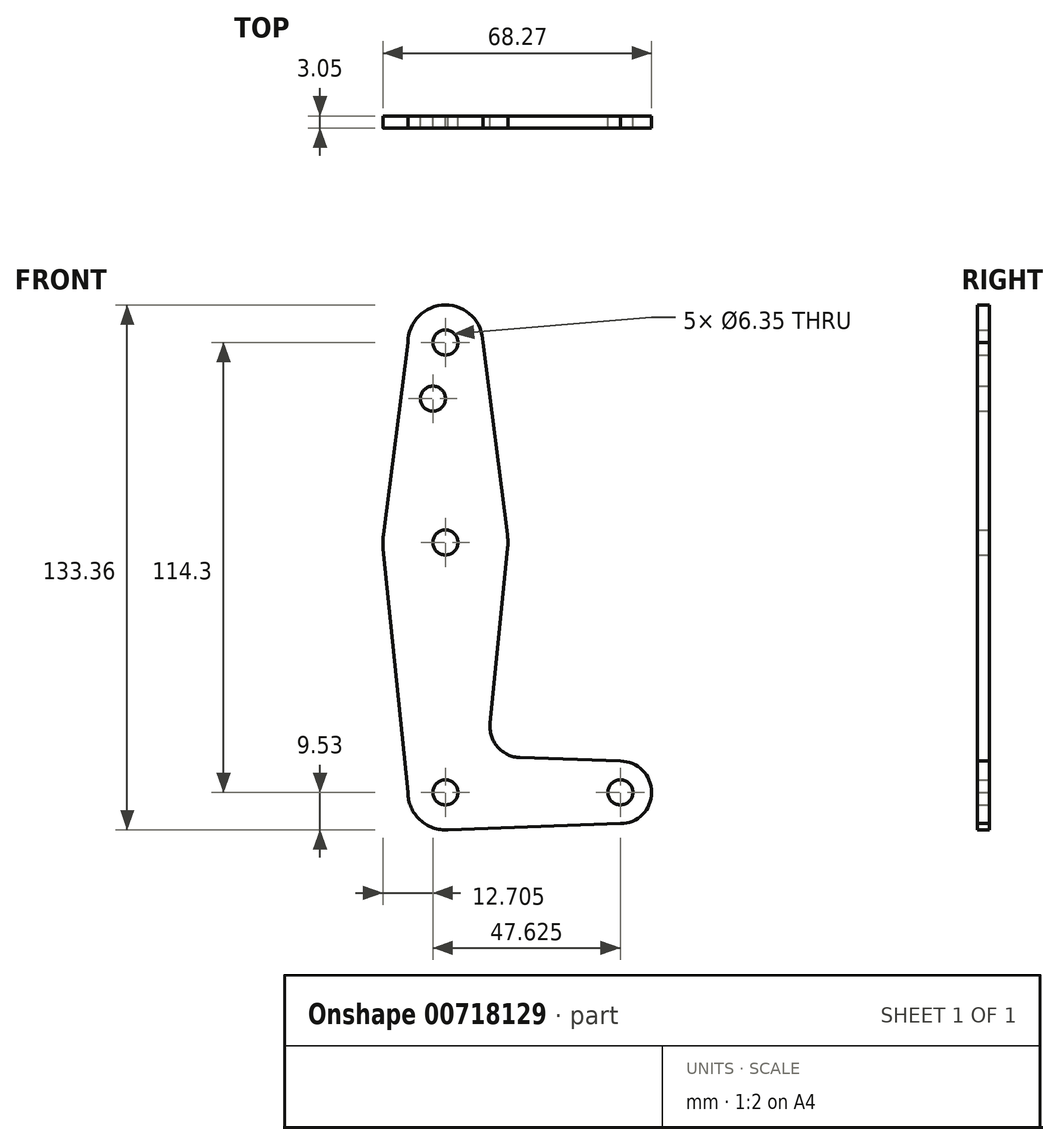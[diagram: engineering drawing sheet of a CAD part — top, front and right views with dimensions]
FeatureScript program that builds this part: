
annotation { "Feature Type Name" : "Feature", "Feature Type Description" : "" }
export const myFeature = defineFeature(function(context is Context, id is Id, definition is map)
    precondition{}
    {
        {
            var Q0;
            Q0=qCreatedBy(makeId("Front.planeOp"),FACE);
            var sketch = newSketch(context, id + "F0", { "sketchPlane" : qUnion([Q0])});
            skLineSegment(sketch, "E0", {"start": v(0, 0) * mm, "end": v(44.45, 0) * mm});
            skLineSegment(sketch, "E1", {"start": v(0, 0) * mm, "end": v(0, 63.5) * mm});
            skLineSegment(sketch, "E2", {"start": v(0, 63.5) * mm, "end": v(0, 114.3) * mm});
            skCircle(sketch, "E3", {"center": v(0, 114.3) * mm, "radius": 9.53 * mm});
            skCircle(sketch, "E4", {"center": v(0, 63.5) * mm, "radius": 15.88 * mm});
            skCircle(sketch, "E5", {"center": v(0, 0) * mm, "radius": 9.53 * mm});
            skCircle(sketch, "E6", {"center": v(44.45, 0) * mm, "radius": 7.94 * mm});
            skLineSegment(sketch, "E7", {"start": v(-9.53, 114.3) * mm, "end": v(-15.75, 65.5) * mm});
            skLineSegment(sketch, "E8", {"start": v(9.53, 114.3) * mm, "end": v(15.75, 65.5) * mm});
            skLineSegment(sketch, "E9", {"start": v(15.8, 61.91) * mm, "end": v(11.34, 17.59) * mm});
            skLineSegment(sketch, "E10", {"start": v(-15.8, 61.91) * mm, "end": v(-9.52, 0) * mm});
            skLineSegment(sketch, "E11", {"start": v(18.97, 8.85) * mm, "end": v(44.45, 7.94) * mm});
            skLineSegment(sketch, "E12", {"start": v(0, -9.53) * mm, "end": v(44.45, -7.94) * mm});
            skCircle(sketch, "E13", {"center": v(-3.18, 100.03) * mm, "radius": 3.18 * mm});
            skCircle(sketch, "E14", {"center": v(0, 114.3) * mm, "radius": 3.18 * mm});
            skCircle(sketch, "E15", {"center": v(0, 63.5) * mm, "radius": 3.18 * mm});
            skCircle(sketch, "E16", {"center": v(0, 0) * mm, "radius": 3.18 * mm});
            skCircle(sketch, "E17", {"center": v(44.45, 0) * mm, "radius": 3.18 * mm});
            skPoint(sketch, "E18.newPointB", {"position": v(9.57, 0) * mm});
            skArc(sketch, "E18.filletArc", {"start": v(11.34, 17.59) * mm, "mid": v(13.26, 11.57) * mm, "end": v(18.97, 8.85) * mm});
            skSolve(sketch);
        }
        {
            var Q0;
            Q0 = qSketchRegion(id + "F0", true);
            var Q1;
            {var subQ0=sQuery(id+"F0.wireOp",EDGE,"E16");var subQ1=sQuery(id+"F0.wireOp",EDGE,"E0");var subQ2=makeQuery(id+"F0.imprint","INTERSECT",VERTEX,{"derivedFrom":[subQ1,subQ0]});Q1=makeQuery(id+"F0.imprint","IMPRINT",FACE,{"disambiguationData":[TD([[makeQuery(id+"F0.imprint","IMPRINT",EDGE,{"disambiguationData":[TD([[subQ2,-1.0]])],"derivedFrom":subQ1}),1.0]])]});}
            extrude(context, id + "F1", {"entities" : qUnion([Q0, Q1]), "depth" : 3.05 * mm, "offsetDistance" : 25.4 * mm});
        }
    });
